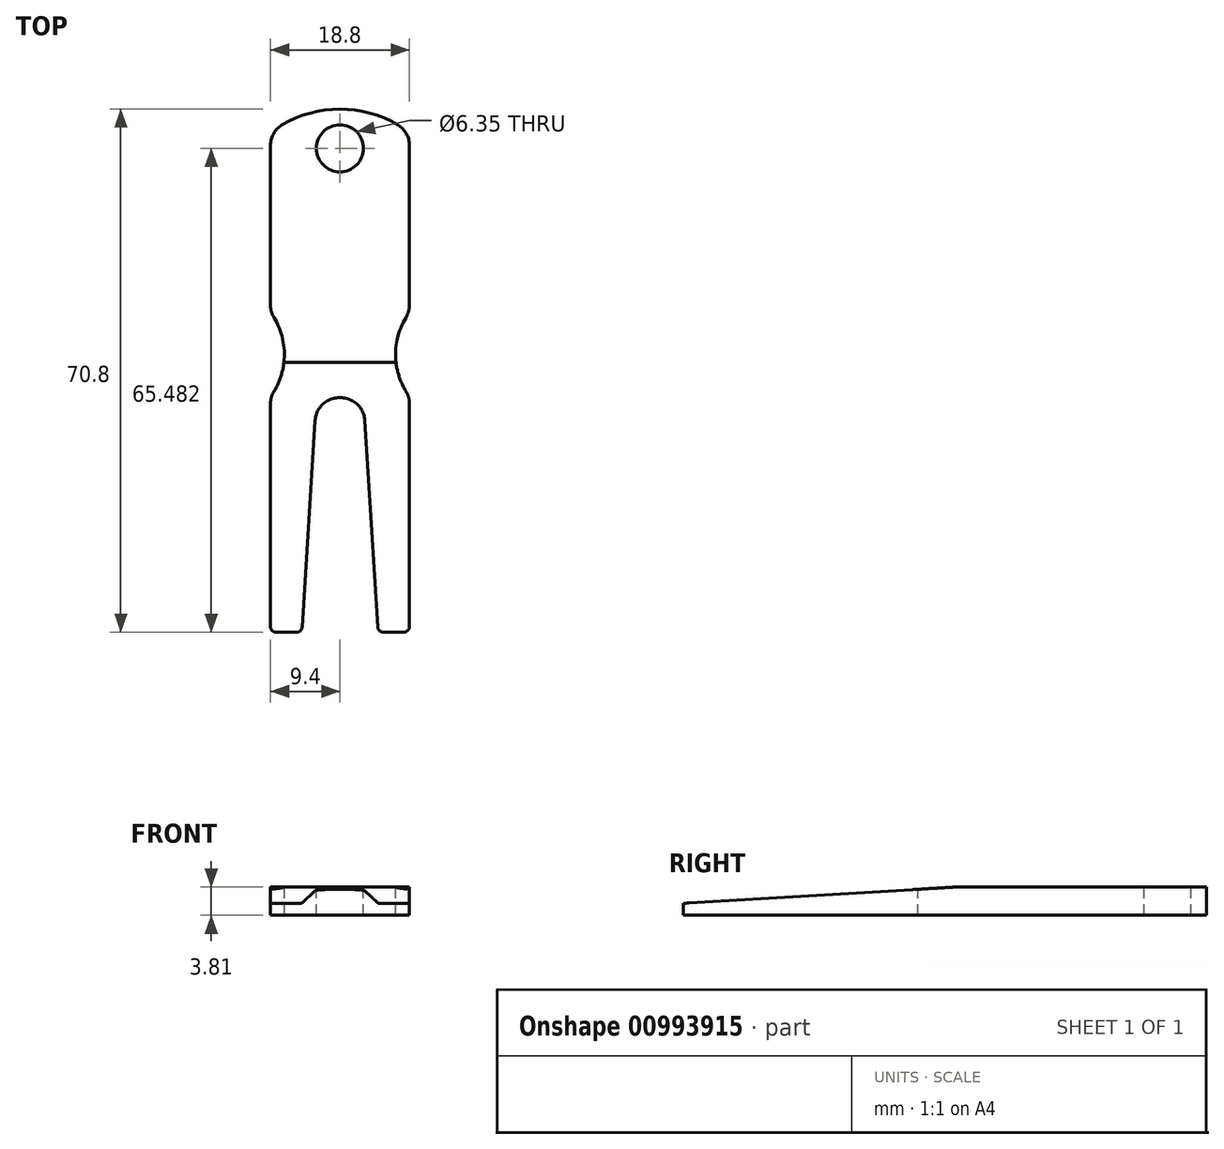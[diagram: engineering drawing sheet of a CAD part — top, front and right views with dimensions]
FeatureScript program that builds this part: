
annotation { "Feature Type Name" : "Feature", "Feature Type Description" : "" }
export const myFeature = defineFeature(function(context is Context, id is Id, definition is map)
    precondition{}
    {
        {
            var Q0;
            Q0=qCreatedBy(makeId("Top.planeOp"),FACE);
            var sketch = newSketch(context, id + "F0", { "sketchPlane" : qUnion([Q0])});
            skArc(sketch, "E0", {"start": v(10.49, -11.06) * mm, "mid": v(0, 15.24) * mm, "end": v(-10.49, -11.06) * mm});
            skLineSegment(sketch, "E1", {"start": v(-5.16, -55.56) * mm, "end": v(-3.17, -23.81) * mm});
            skLineSegment(sketch, "E2", {"start": v(-3.17, -23.81) * mm, "end": v(3.18, -23.81) * mm});
            skLineSegment(sketch, "E3", {"start": v(3.17, -23.81) * mm, "end": v(5.16, -55.56) * mm});
            skArc(sketch, "E4", {"start": v(10.49, -11.06) * mm, "mid": v(7.6, -16.73) * mm, "end": v(8.93, -22.95) * mm});
            skArc(sketch, "E5", {"start": v(-8.93, -22.95) * mm, "mid": v(-7.6, -16.73) * mm, "end": v(-10.49, -11.06) * mm});
            skPoint(sketch, "E6.visualSharp", {"position": v(-9.53, -23.81) * mm});
            skArc(sketch, "E6.filletArc", {"start": v(-8.93, -22.95) * mm, "mid": v(-9.28, -23.75) * mm, "end": v(-9.4, -24.61) * mm});
            skPoint(sketch, "E7.visualSharp", {"position": v(9.53, -23.81) * mm});
            skArc(sketch, "E7.filletArc", {"start": v(9.4, -24.61) * mm, "mid": v(9.28, -23.75) * mm, "end": v(8.93, -22.95) * mm});
            skLineSegment(sketch, "E8", {"start": v(9.4, -24.61) * mm, "end": v(9.4, -55.56) * mm});
            skLineSegment(sketch, "E9", {"start": v(-9.4, -24.61) * mm, "end": v(-9.4, -55.56) * mm});
            skLineSegment(sketch, "E10", {"start": v(-9.4, -55.56) * mm, "end": v(-5.16, -55.56) * mm});
            skLineSegment(sketch, "E11", {"start": v(5.16, -55.56) * mm, "end": v(9.4, -55.56) * mm});
            skCircle(sketch, "E12", {"center": v(0, 9.92) * mm, "radius": 3.18 * mm});
            skSolve(sketch);
        }
        {
            var Q0;
            Q0 = qSketchRegion(id + "F0", true);
            extrude(context, id + "F1", {"entities" : qUnion([Q0]), "oppositeDirection" : true, "depth" : 3.8 * mm, "offsetDistance" : 25.4 * mm});
        }
        {
            var Q0;
            Q0=makeQuery(id+"F1.opExtrude","SWEPT_EDGE",EDGE,{"disambiguationData":[OSD([sQuery(id+"F0.wireOp",EDGE,"E1"),sQuery(id+"F0.wireOp",EDGE,"E2")])]});
            var Q1;
            Q1=makeQuery(id+"F1.opExtrude","SWEPT_EDGE",EDGE,{"disambiguationData":[OSD([sQuery(id+"F0.wireOp",EDGE,"E2"),sQuery(id+"F0.wireOp",EDGE,"E3")])]});
            fillet(context, id + "F2", {"entities" : qUnion([Q0, Q1]), "radius" : 3.3 * mm, "tangentPropagation" : true, "allowEdgeOverflow" : false});
        }
        {
            var Q0;
            Q0=makeQuery(id+"F1.opExtrude","SWEPT_EDGE",EDGE,{"disambiguationData":[OSD([sQuery(id+"F0.wireOp",EDGE,"E3"),sQuery(id+"F0.wireOp",EDGE,"zIxWqQ5P-xl6n-nnnS-UIE0-HVxdHsykupnp")])]});
            var Q1;
            Q1=makeQuery(id+"F1.opExtrude","SWEPT_EDGE",EDGE,{"disambiguationData":[OSD([sQuery(id+"F0.wireOp",EDGE,"FaElaQVg-0aIf-zFK8-XIk3-84AHfUqppdYG"),sQuery(id+"F0.wireOp",EDGE,"E1")])]});
            var Q2;
            Q2=makeQuery(id+"F1.opExtrude","SWEPT_EDGE",EDGE,{"disambiguationData":[OSD([sQuery(id+"F0.wireOp",EDGE,"E8"),sQuery(id+"F0.wireOp",EDGE,"E11")])]});
            var Q3;
            Q3=makeQuery(id+"F1.opExtrude","SWEPT_EDGE",EDGE,{"disambiguationData":[OSD([sQuery(id+"F0.wireOp",EDGE,"E9"),sQuery(id+"F0.wireOp",EDGE,"E10")])]});
            fillet(context, id + "F3", {"entities" : qUnion([Q0, Q1, Q2, Q3]), "radius" : 0.76 * mm, "tangentPropagation" : true, "allowEdgeOverflow" : false});
        }
        {
            var Q0;
            Q0=makeQuery(id+"F1.opExtrude","CAP_FACE",FACE,{"disambiguationData":[OSD([sQuery(id+"F0.wireOp",EDGE,"E0"),sQuery(id+"F0.wireOp",EDGE,"FaElaQVg-0aIf-zFK8-XIk3-84AHfUqppdYG"),sQuery(id+"F0.wireOp",EDGE,"E1"),sQuery(id+"F0.wireOp",EDGE,"E2"),sQuery(id+"F0.wireOp",EDGE,"E3"),sQuery(id+"F0.wireOp",EDGE,"zIxWqQ5P-xl6n-nnnS-UIE0-HVxdHsykupnp"),sQuery(id+"F0.wireOp",EDGE,"E4"),sQuery(id+"F0.wireOp",EDGE,"E5"),sQuery(id+"F0.wireOp",EDGE,"E6.filletArc"),sQuery(id+"F0.wireOp",EDGE,"E7.filletArc")])],"isStart":true});
            var sketch = newSketch(context, id + "F4", { "sketchPlane" : qUnion([Q0])});
            skLineSegment(sketch, "E13", {"start": v(-9.4, 17.78) * mm, "end": v(-9.4, -15.88) * mm});
            skLineSegment(sketch, "E14", {"start": v(9.4, 17.78) * mm, "end": v(9.4, -15.88) * mm});
            skLineSegment(sketch, "E15", {"start": v(9.4, -15.88) * mm, "end": v(19.05, -15.88) * mm});
            skLineSegment(sketch, "E16", {"start": v(19.05, -15.88) * mm, "end": v(19.05, 20.32) * mm});
            skLineSegment(sketch, "E17", {"start": v(19.05, 20.32) * mm, "end": v(-19.05, 20.32) * mm});
            skLineSegment(sketch, "E18", {"start": v(-19.05, 20.32) * mm, "end": v(-19.05, -15.88) * mm});
            skLineSegment(sketch, "E19", {"start": v(-19.05, -15.88) * mm, "end": v(-9.4, -15.88) * mm});
            skLineSegment(sketch, "E20", {"start": v(-9.4, 17.78) * mm, "end": v(9.4, 17.78) * mm});
            skSolve(sketch);
        }
        {
            var Q0;
            Q0 = qSketchRegion(id + "F4", true);
            extrude(context, id + "F5", {"entities" : qUnion([Q0]), "operationType" : NewBodyOperationType.REMOVE, "endBound" : BoundingType.THROUGH_ALL, "oppositeDirection" : true, "depth" : 25.4 * mm, "offsetDistance" : 25.4 * mm});
        }
        {
            var Q0;
            Q0=makeQuery(id+"F5.boolean.opBoolean","INTERSECT",EDGE,{"derivedFrom":[makeQuery(id+"F1.opExtrude","SWEPT_FACE",FACE,{"disambiguationData":[OSD([sQuery(id+"F0.wireOp",EDGE,"E0")])]}),makeQuery(id+"F5.opExtrude","SWEPT_FACE",FACE,{"disambiguationData":[OSD([sQuery(id+"F4.wireOp",EDGE,"E14")])]})]});
            var Q1;
            Q1=makeQuery(id+"F5.boolean.opBoolean","INTERSECT",EDGE,{"derivedFrom":[makeQuery(id+"F1.opExtrude","SWEPT_FACE",FACE,{"disambiguationData":[OSD([sQuery(id+"F0.wireOp",EDGE,"E0")])]}),makeQuery(id+"F5.opExtrude","SWEPT_FACE",FACE,{"disambiguationData":[OSD([sQuery(id+"F4.wireOp",EDGE,"E13")])]})]});
            var Q2;
            Q2=makeQuery(id+"F5.boolean.opBoolean","INTERSECT",EDGE,{"derivedFrom":[makeQuery(id+"F1.opExtrude","SWEPT_FACE",FACE,{"disambiguationData":[OSD([sQuery(id+"F0.wireOp",EDGE,"E5")])]}),makeQuery(id+"F5.opExtrude","SWEPT_FACE",FACE,{"disambiguationData":[OSD([sQuery(id+"F4.wireOp",EDGE,"E13")])]})]});
            var Q3;
            Q3=makeQuery(id+"F5.boolean.opBoolean","INTERSECT",EDGE,{"derivedFrom":[makeQuery(id+"F1.opExtrude","SWEPT_FACE",FACE,{"disambiguationData":[OSD([sQuery(id+"F0.wireOp",EDGE,"E4")])]}),makeQuery(id+"F5.opExtrude","SWEPT_FACE",FACE,{"disambiguationData":[OSD([sQuery(id+"F4.wireOp",EDGE,"E14")])]})]});
            fillet(context, id + "F6", {"entities" : qUnion([Q0, Q1, Q2, Q3]), "radius" : 3.17 * mm, "tangentPropagation" : true, "allowEdgeOverflow" : false});
        }
        {
            var Q0;
            Q0=makeQuery(id+"F5.boolean.opBoolean","COPY",FACE,{"derivedFrom":makeQuery(id+"F5.opExtrude","SWEPT_FACE",FACE,{"disambiguationData":[OSD([sQuery(id+"F4.wireOp",EDGE,"E14")])]})});
            var sketch = newSketch(context, id + "F7", { "sketchPlane" : qUnion([Q0])});
            skLineSegment(sketch, "E21", {"start": v(-57.15, -2.29) * mm, "end": v(-19.05, 0) * mm});
            skLineSegment(sketch, "E22", {"start": v(-19.05, 0) * mm, "end": v(-57.15, 0) * mm});
            skLineSegment(sketch, "E23", {"start": v(-57.15, 0) * mm, "end": v(-57.15, -2.29) * mm});
            skSolve(sketch);
        }
        {
            var Q0;
            Q0 = qSketchRegion(id + "F7", true);
            extrude(context, id + "F8", {"entities" : qUnion([Q0]), "operationType" : NewBodyOperationType.REMOVE, "endBound" : BoundingType.THROUGH_ALL, "oppositeDirection" : true, "depth" : 25.4 * mm, "offsetDistance" : 25.4 * mm});
        }
    });
